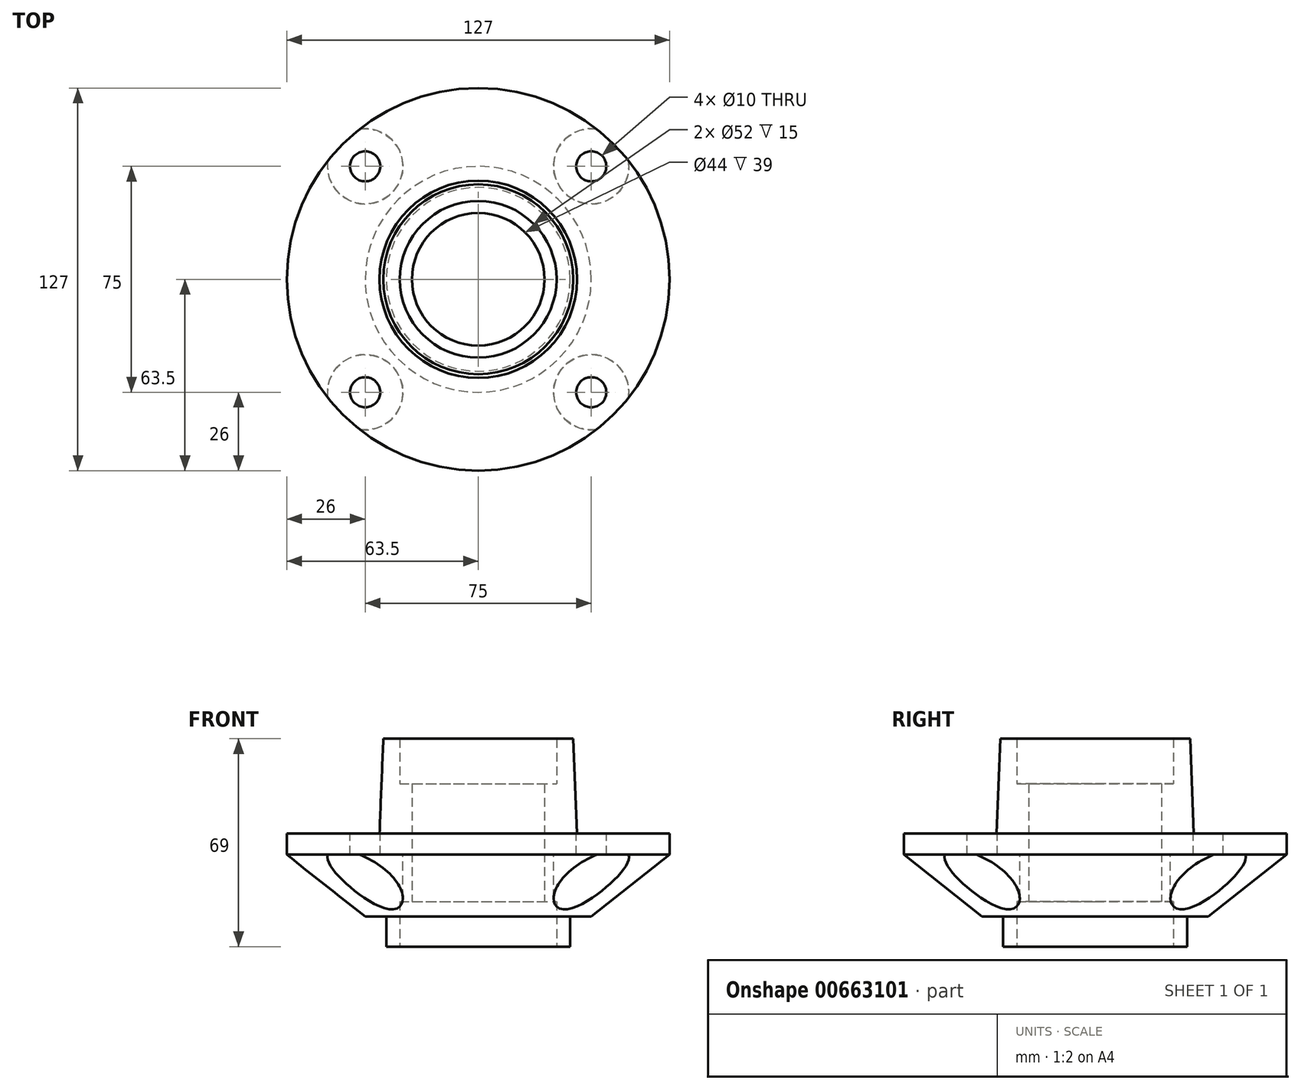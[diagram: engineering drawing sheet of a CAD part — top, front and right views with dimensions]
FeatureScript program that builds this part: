
annotation { "Feature Type Name" : "Feature", "Feature Type Description" : "" }
export const myFeature = defineFeature(function(context is Context, id is Id, definition is map)
    precondition{}
    {
        {
            var Q0;
            Q0=qCreatedBy(makeId("Top.planeOp"),FACE);
            var sketch = newSketch(context, id + "F0", { "sketchPlane" : qUnion([Q0])});
            skLineSegment(sketch, "E0.bottom", {"start": v(-37.5, 37.5) * mm, "end": v(37.5, 37.5) * mm, "construction": true});
            skLineSegment(sketch, "E0.top", {"start": v(-37.5, -37.5) * mm, "end": v(37.5, -37.5) * mm, "construction": true});
            skLineSegment(sketch, "E0.left", {"start": v(-37.5, 37.5) * mm, "end": v(-37.5, -37.5) * mm, "construction": true});
            skLineSegment(sketch, "E0.right", {"start": v(37.5, 37.5) * mm, "end": v(37.5, -37.5) * mm, "construction": true});
            skLineSegment(sketch, "E1", {"start": v(0, 0) * mm, "end": v(37.5, 0) * mm, "construction": true});
            skLineSegment(sketch, "E2", {"start": v(0, 0) * mm, "end": v(-37.5, 0) * mm, "construction": true});
            skLineSegment(sketch, "E3", {"start": v(0, 0) * mm, "end": v(0, 37.5) * mm, "construction": true});
            skCircle(sketch, "E4", {"center": v(0, 0) * mm, "radius": 63.5 * mm});
            skCircle(sketch, "E5", {"center": v(-37.5, 37.5) * mm, "radius": 5 * mm});
            skCircle(sketch, "E6", {"center": v(37.5, 37.5) * mm, "radius": 5 * mm});
            skCircle(sketch, "E7", {"center": v(37.5, -37.5) * mm, "radius": 5 * mm});
            skCircle(sketch, "E8", {"center": v(-37.5, -37.5) * mm, "radius": 5 * mm});
            skSolve(sketch);
        }
        {
            var Q0;
            Q0=qCreatedBy(makeId("Front.planeOp"),FACE);
            var sketch = newSketch(context, id + "F1", { "sketchPlane" : qUnion([Q0])});
            skLineSegment(sketch, "E9", {"start": v(0, 0) * mm, "end": v(0, 60.76) * mm, "construction": true});
            skLineSegment(sketch, "E10", {"start": v(-32.75, 0) * mm, "end": v(-31.5, 31.5) * mm});
            skLineSegment(sketch, "E11", {"start": v(-31.5, 31.5) * mm, "end": v(-26, 31.5) * mm});
            skLineSegment(sketch, "E12", {"start": v(-63.5, -7) * mm, "end": v(-63.5, 0) * mm});
            skLineSegment(sketch, "E13", {"start": v(-63.5, 0) * mm, "end": v(-32.75, 0) * mm});
            skLineSegment(sketch, "E14", {"start": v(-26, 31.5) * mm, "end": v(-26, 16.5) * mm});
            skLineSegment(sketch, "E15", {"start": v(-26, 16.5) * mm, "end": v(-22, 16.5) * mm});
            skLineSegment(sketch, "E16", {"start": v(-22, 16.5) * mm, "end": v(-22, -22.5) * mm});
            skLineSegment(sketch, "E17", {"start": v(-22, -22.5) * mm, "end": v(-26, -22.5) * mm});
            skLineSegment(sketch, "E18", {"start": v(-26, -22.5) * mm, "end": v(-26, -37.5) * mm});
            skLineSegment(sketch, "E19", {"start": v(-26, 16.5) * mm, "end": v(-26, -22.5) * mm, "construction": true});
            skLineSegment(sketch, "E20", {"start": v(-30.5, -37.5) * mm, "end": v(-30.5, -27.5) * mm});
            skLineSegment(sketch, "E21", {"start": v(-30.5, -27.5) * mm, "end": v(-37.5, -27.5) * mm});
            skLineSegment(sketch, "E22", {"start": v(-30.5, -37.5) * mm, "end": v(-26, -37.5) * mm});
            skLineSegment(sketch, "E23", {"start": v(-37.5, -27.5) * mm, "end": v(-63.5, -7) * mm});
            skSolve(sketch);
        }
        {
            var Q0;
            Q0 = qSketchRegion(id + "F1", true);
            var Q1;
            Q1=sQuery(id+"F1.wireOp",EDGE,"E9");
            revolve(context, id + "F2", {"surfaceOperationType" : NewSurfaceOperationType.NEW, "entities" : qUnion([Q0]), "axis" : qUnion([Q1]), "revolveType" : RevolveType.FULL});
        }
        {
            var Q0;
            Q0=makeQuery(id+"F0.imprint","IMPRINT",FACE,{"disambiguationData":[TD([[makeQuery(id+"F0.imprint","IMPRINT",EDGE,{"derivedFrom":sQuery(id+"F0.wireOp",EDGE,"E5")}),1.0]])]});
            var Q1;
            Q1=makeQuery(id+"F0.imprint","IMPRINT",FACE,{"disambiguationData":[TD([[makeQuery(id+"F0.imprint","IMPRINT",EDGE,{"derivedFrom":sQuery(id+"F0.wireOp",EDGE,"E8")}),1.0]])]});
            var Q2;
            Q2=makeQuery(id+"F0.imprint","IMPRINT",FACE,{"disambiguationData":[TD([[makeQuery(id+"F0.imprint","IMPRINT",EDGE,{"derivedFrom":sQuery(id+"F0.wireOp",EDGE,"E7")}),1.0]])]});
            var Q3;
            Q3=makeQuery(id+"F0.imprint","IMPRINT",FACE,{"disambiguationData":[TD([[makeQuery(id+"F0.imprint","IMPRINT",EDGE,{"derivedFrom":sQuery(id+"F0.wireOp",EDGE,"E6")}),1.0]])]});
            var Q4;
            Q4=sQuery(id+"F0.wireOp",EDGE,"E5");
            var Q5;
            Q5=sQuery(id+"F0.wireOp",EDGE,"E7");
            var Q6;
            Q6=sQuery(id+"F0.wireOp",EDGE,"E8");
            var Q7;
            Q7=sQuery(id+"F0.wireOp",EDGE,"E6");
            extrude(context, id + "F3", {"entities" : qUnion([Q0, Q1, Q2, Q3]), "operationType" : NewBodyOperationType.REMOVE, "surfaceEntities" : qUnion([Q4, Q5, Q6, Q7]), "oppositeDirection" : true, "depth" : 25 * mm, "offsetDistance" : 25 * mm});
        }
        {
            var Q0;
            Q0=qCreatedBy(makeId("Top.planeOp"),FACE);
            cPlane(context, id + "F4", {"entities" : qUnion([Q0]), "cplaneType" : CPlaneType.OFFSET, "offset" : 7 * mm, "oppositeDirection" : true, "width" : 150 * mm, "height" : 150 * mm});
        }
        {
            var Q0;
            Q0=qCreatedBy(id+"F4.planeOp",FACE);
            var sketch = newSketch(context, id + "F5", { "sketchPlane" : qUnion([Q0])});
            skCircle(sketch, "E24.0", {"center": v(37.5, 37.5) * mm, "radius": 5 * mm, "construction": true});
            skCircle(sketch, "E25.0", {"center": v(37.5, -37.5) * mm, "radius": 5 * mm, "construction": true});
            skCircle(sketch, "E26.0", {"center": v(-37.5, -37.5) * mm, "radius": 5 * mm, "construction": true});
            skCircle(sketch, "E27.0", {"center": v(-37.5, 37.5) * mm, "radius": 5 * mm, "construction": true});
            skCircle(sketch, "E28", {"center": v(-37.5, 37.5) * mm, "radius": 12.5 * mm});
            skCircle(sketch, "E29", {"center": v(37.5, 37.5) * mm, "radius": 12.5 * mm});
            skCircle(sketch, "E30", {"center": v(-37.5, -37.5) * mm, "radius": 12.5 * mm});
            skCircle(sketch, "E31", {"center": v(37.5, -37.5) * mm, "radius": 12.5 * mm});
            skSolve(sketch);
        }
        {
            var Q0;
            Q0 = qSketchRegion(id + "F5", true);
            extrude(context, id + "F6", {"entities" : qUnion([Q0]), "operationType" : NewBodyOperationType.REMOVE, "oppositeDirection" : true, "depth" : 25 * mm, "offsetDistance" : 25 * mm});
        }
    });
